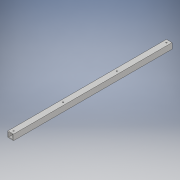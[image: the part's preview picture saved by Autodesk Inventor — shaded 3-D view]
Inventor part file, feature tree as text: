
AUTODESK INVENTOR PART (.ipt)
format: ipt  version: 2019 (Build 230136000, 136)  size: 124,928 bytes
history: native  units: in
note: dims shown in document units (in); Inventor stores cm internally (conversion verified against a paired STEP export)
features: extrude x3, sketch x3
ambient origin geometry x8: Origin, YZ Plane, XZ Plane, XY Plane, X Axis, Y Axis, Z Axis, Center Point
bodies: Solid1 (feature_tree)
feature tree (6):
  extrude  "Extrusion1"  Depth=1.0in
  extrude  "Extrusion2"  Depth=28.0in
  extrude  "Extrusion3"  Depth=0.125in
  sketch  "Sketch1"  dims[d0=1.0in d1=1.0in]
  sketch  "Sketch2"  dims[d2=28.0in d3=0.0in d4=0.5in]
  sketch  "Sketch3"  dims[d5=0.2031in d6=9.25in d7=0.2031in d8=28.0in d9=0.0in d10=0.125in d11=30.0in d12=0.0in]
